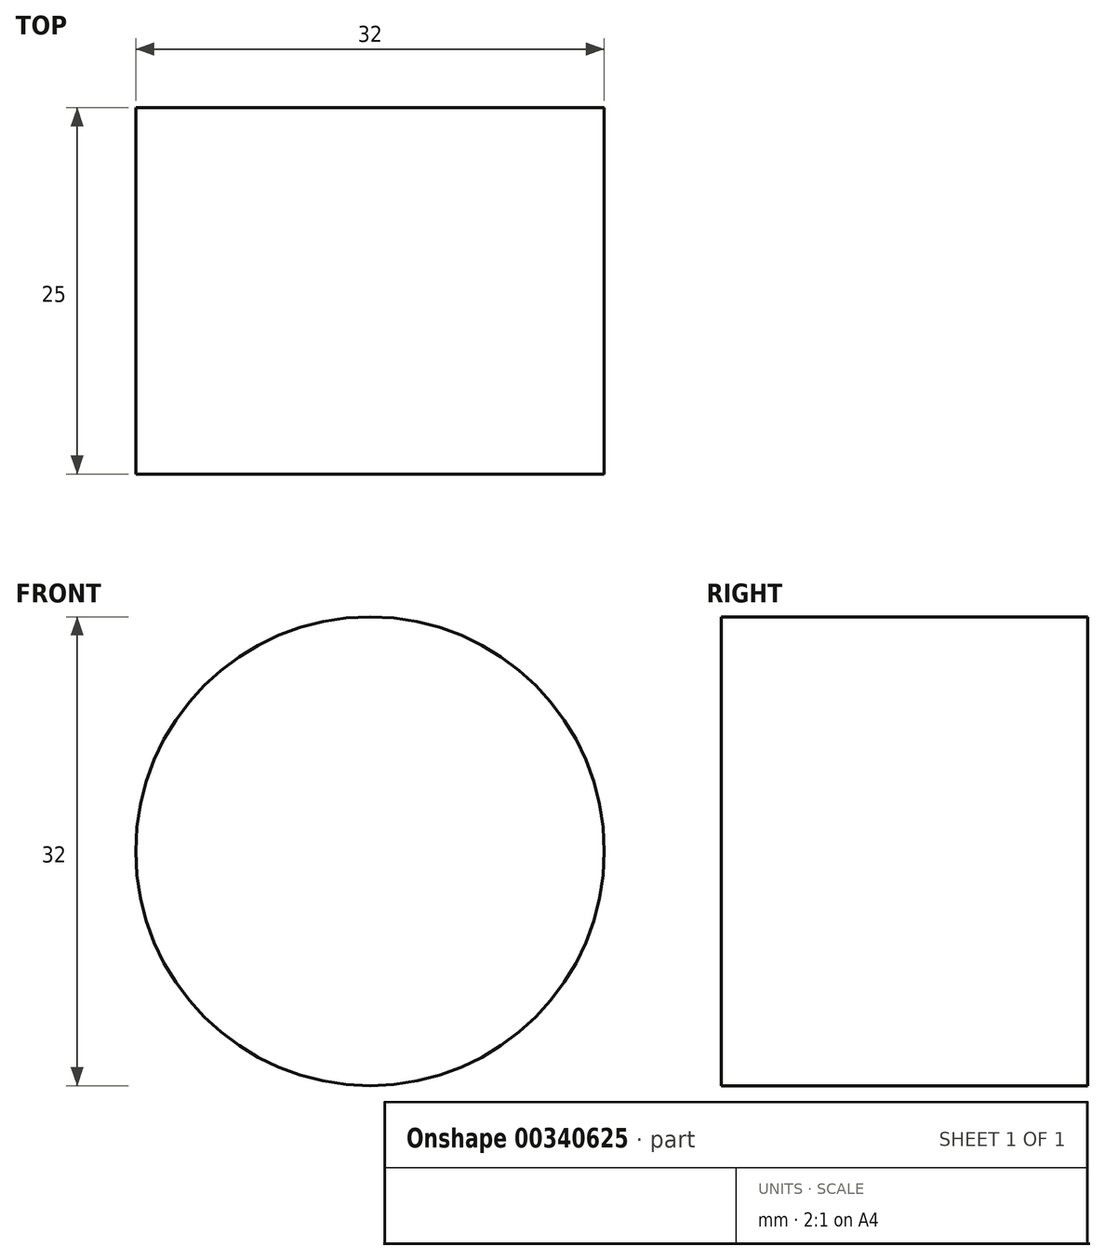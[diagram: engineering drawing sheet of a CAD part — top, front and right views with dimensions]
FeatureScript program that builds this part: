
annotation { "Feature Type Name" : "Feature", "Feature Type Description" : "" }
export const myFeature = defineFeature(function(context is Context, id is Id, definition is map)
    precondition{}
    {
        {
            var Q0;
            Q0=qCreatedBy(makeId("Front.planeOp"),FACE);
            var sketch = newSketch(context, id + "F0", { "sketchPlane" : qUnion([Q0])});
            skCircle(sketch, "E0", {"center": v(-42.3, 32.98) * mm, "radius": 16 * mm});
            skSolve(sketch);
        }
        {
            var Q0;
            Q0 = qSketchRegion(id + "F0", true);
            extrude(context, id + "F1", {"entities" : qUnion([Q0]), "depth" : 25 * mm});
        }
    });
